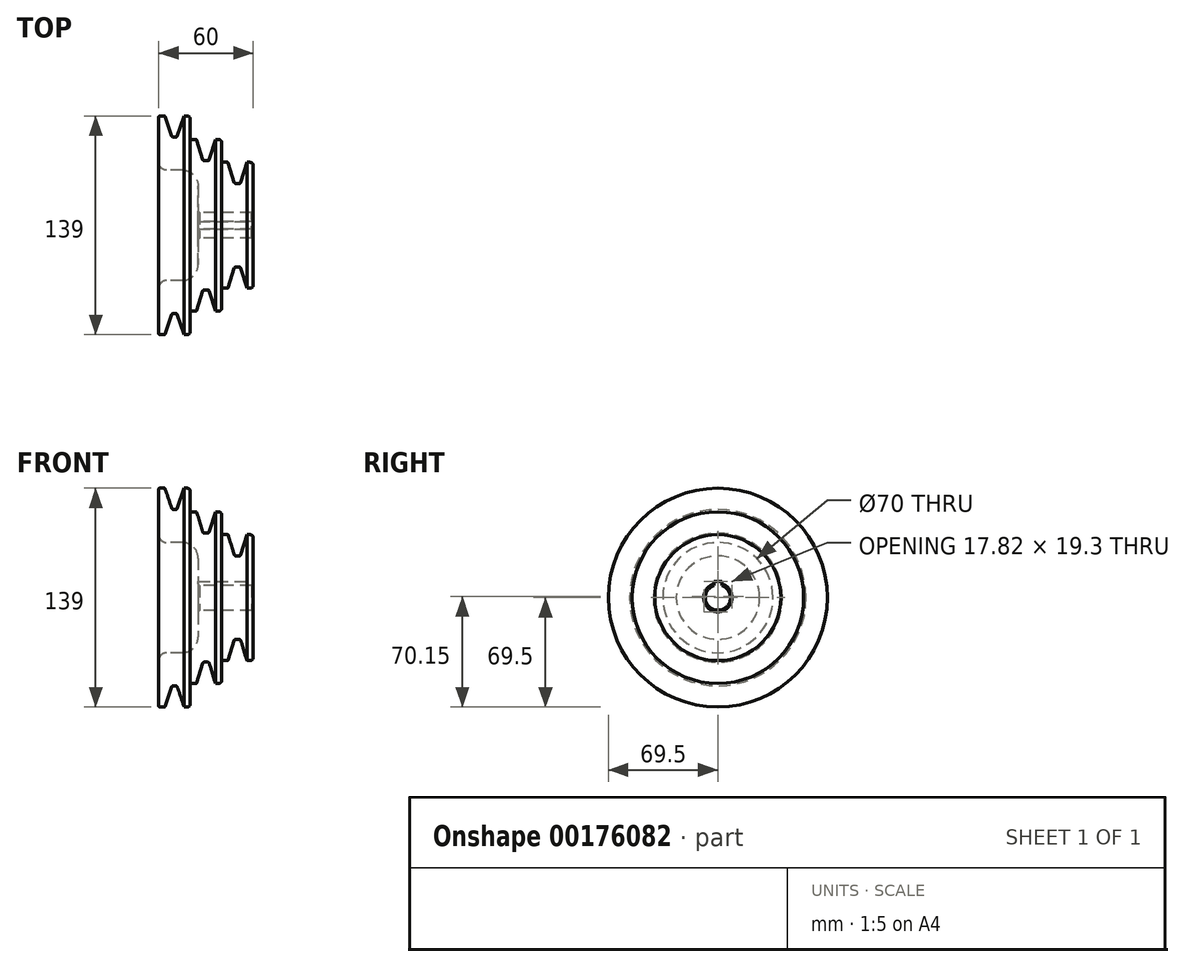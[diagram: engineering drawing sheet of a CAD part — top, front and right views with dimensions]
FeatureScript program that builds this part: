
annotation { "Feature Type Name" : "Feature", "Feature Type Description" : "" }
export const myFeature = defineFeature(function(context is Context, id is Id, definition is map)
    precondition{}
    {
        {
            var Q0;
            Q0=qCreatedBy(makeId("Front.planeOp"),FACE);
            var sketch = newSketch(context, id + "F0", { "sketchPlane" : qUnion([Q0])});
            skLineSegment(sketch, "E0", {"start": v(60, 8) * mm, "end": v(25, 8) * mm});
            skLineSegment(sketch, "E1", {"start": v(25, 8) * mm, "end": v(25, 35) * mm});
            skLineSegment(sketch, "E2", {"start": v(25, 35) * mm, "end": v(0, 35) * mm});
            skLineSegment(sketch, "E3", {"start": v(0, 35) * mm, "end": v(0, 69.5) * mm});
            skLineSegment(sketch, "E4", {"start": v(0, 69.5) * mm, "end": v(20, 69.5) * mm});
            skLineSegment(sketch, "E5", {"start": v(20, 69.5) * mm, "end": v(20, 54.5) * mm});
            skLineSegment(sketch, "E6", {"start": v(20, 54.5) * mm, "end": v(40, 54.5) * mm});
            skLineSegment(sketch, "E7", {"start": v(40, 54.5) * mm, "end": v(40, 40) * mm});
            skLineSegment(sketch, "E8", {"start": v(40, 40) * mm, "end": v(60, 40) * mm});
            skLineSegment(sketch, "E9", {"start": v(60, 40) * mm, "end": v(60, 8) * mm});
            skLineSegment(sketch, "E10", {"start": v(0, 0) * mm, "end": v(60.5, 0) * mm});
            skSolve(sketch);
        }
        {
            var Q0;
            Q0 = qSketchRegion(id + "F0", true);
            var Q1;
            Q1=sQuery(id+"F0.wireOp",EDGE,"E10");
            revolve(context, id + "F1", {"entities" : qUnion([Q0]), "axis" : qUnion([Q1]), "revolveType" : RevolveType.FULL});
        }
        {
            var Q0;
            Q0=qCreatedBy(makeId("Front.planeOp"),FACE);
            var sketch = newSketch(context, id + "F2", { "sketchPlane" : qUnion([Q0])});
            skLineSegment(sketch, "E11", {"start": v(3.85, 69.5) * mm, "end": v(16.15, 69.5) * mm});
            skLineSegment(sketch, "E12", {"start": v(16.15, 69.5) * mm, "end": v(11.5, 56) * mm});
            skLineSegment(sketch, "E13", {"start": v(11.5, 56) * mm, "end": v(8.5, 56) * mm});
            skLineSegment(sketch, "E14", {"start": v(8.5, 56) * mm, "end": v(3.85, 69.5) * mm});
            skLineSegment(sketch, "E15", {"start": v(10, 69.5) * mm, "end": v(10, 56) * mm});
            skLineSegment(sketch, "E16", {"start": v(5.4, 65) * mm, "end": v(14.6, 65) * mm});
            skLineSegment(sketch, "E17", {"start": v(0, 0) * mm, "end": v(23.75, 0) * mm});
            skSolve(sketch);
        }
        {
            var Q0;
            Q0 = qSketchRegion(id + "F2", true);
            var Q1;
            Q1=sQuery(id+"F2.wireOp",EDGE,"E17");
            revolve(context, id + "F3", {"operationType" : NewBodyOperationType.REMOVE, "entities" : qUnion([Q0]), "axis" : qUnion([Q1]), "revolveType" : RevolveType.FULL, "oppositeDirection" : true});
        }
        {
            var Q0;
            Q0=qCreatedBy(makeId("Front.planeOp"),FACE);
            var sketch = newSketch(context, id + "F4", { "sketchPlane" : qUnion([Q0])});
            skLineSegment(sketch, "E18", {"start": v(24.02, 54.5) * mm, "end": v(35.98, 54.5) * mm});
            skLineSegment(sketch, "E19", {"start": v(35.98, 54.5) * mm, "end": v(31.85, 41) * mm});
            skLineSegment(sketch, "E20", {"start": v(31.85, 41) * mm, "end": v(28.15, 41) * mm});
            skLineSegment(sketch, "E21", {"start": v(28.15, 41) * mm, "end": v(24.02, 54.5) * mm});
            skLineSegment(sketch, "E22", {"start": v(30, 54.5) * mm, "end": v(30, 41) * mm});
            skLineSegment(sketch, "E23", {"start": v(25.4, 50) * mm, "end": v(34.6, 50) * mm});
            skLineSegment(sketch, "E24", {"start": v(0, 0) * mm, "end": v(40.75, 0) * mm});
            skSolve(sketch);
        }
        {
            var Q0;
            Q0 = qSketchRegion(id + "F4", true);
            var Q1;
            Q1=sQuery(id+"F4.wireOp",EDGE,"E24");
            revolve(context, id + "F5", {"operationType" : NewBodyOperationType.REMOVE, "entities" : qUnion([Q0]), "axis" : qUnion([Q1]), "revolveType" : RevolveType.FULL});
        }
        {
            var Q0;
            Q0=qCreatedBy(makeId("Front.planeOp"),FACE);
            var sketch = newSketch(context, id + "F6", { "sketchPlane" : qUnion([Q0])});
            skLineSegment(sketch, "E25", {"start": v(44.02, 40) * mm, "end": v(55.98, 40) * mm});
            skLineSegment(sketch, "E26", {"start": v(55.98, 40) * mm, "end": v(51.85, 26.5) * mm});
            skLineSegment(sketch, "E27", {"start": v(51.85, 26.5) * mm, "end": v(48.15, 26.5) * mm});
            skLineSegment(sketch, "E28", {"start": v(48.15, 26.5) * mm, "end": v(44.02, 40) * mm});
            skLineSegment(sketch, "E29", {"start": v(50, 40) * mm, "end": v(50, 26.5) * mm});
            skLineSegment(sketch, "E30", {"start": v(45.4, 35.5) * mm, "end": v(54.6, 35.5) * mm});
            skLineSegment(sketch, "E31", {"start": v(0, 0) * mm, "end": v(19.74, 0) * mm});
            skSolve(sketch);
        }
        {
            var Q0;
            Q0 = qSketchRegion(id + "F6", true);
            var Q1;
            Q1=sQuery(id+"F6.wireOp",EDGE,"E31");
            revolve(context, id + "F7", {"operationType" : NewBodyOperationType.REMOVE, "entities" : qUnion([Q0]), "axis" : qUnion([Q1]), "revolveType" : RevolveType.FULL, "oppositeDirection" : true});
        }
        {
            var Q0;
            Q0=makeQuery(id+"F1.opRevolve","SWEPT_EDGE",EDGE,{"disambiguationData":[OSD([sQuery(id+"F0.wireOp",EDGE,"E3"),sQuery(id+"F0.wireOp",EDGE,"E4")])]});
            var Q1;
            Q1=makeQuery(id+"F3.boolean.opBoolean","COPY",EDGE,{"derivedFrom":makeQuery(id+"F3.opRevolve","SWEPT_EDGE",EDGE,{"disambiguationData":[OSD([sQuery(id+"F2.wireOp",EDGE,"E11"),sQuery(id+"F2.wireOp",EDGE,"E14")])]})});
            var Q2;
            Q2=makeQuery(id+"F3.boolean.opBoolean","COPY",EDGE,{"derivedFrom":makeQuery(id+"F3.opRevolve","SWEPT_EDGE",EDGE,{"disambiguationData":[OSD([sQuery(id+"F2.wireOp",EDGE,"E11"),sQuery(id+"F2.wireOp",EDGE,"E12")])]})});
            var Q3;
            Q3=makeQuery(id+"F1.opRevolve","SWEPT_EDGE",EDGE,{"disambiguationData":[OSD([sQuery(id+"F0.wireOp",EDGE,"E5"),sQuery(id+"F0.wireOp",EDGE,"E6")])]});
            var Q4;
            Q4=makeQuery(id+"F5.boolean.opBoolean","COPY",EDGE,{"derivedFrom":makeQuery(id+"F5.opRevolve","SWEPT_EDGE",EDGE,{"disambiguationData":[OSD([sQuery(id+"F4.wireOp",EDGE,"E18"),sQuery(id+"F4.wireOp",EDGE,"E21")])]})});
            var Q5;
            Q5=makeQuery(id+"F5.boolean.opBoolean","COPY",EDGE,{"derivedFrom":makeQuery(id+"F5.opRevolve","SWEPT_EDGE",EDGE,{"disambiguationData":[OSD([sQuery(id+"F4.wireOp",EDGE,"E18"),sQuery(id+"F4.wireOp",EDGE,"E19")])]})});
            var Q6;
            Q6=makeQuery(id+"F1.opRevolve","SWEPT_EDGE",EDGE,{"disambiguationData":[OSD([sQuery(id+"F0.wireOp",EDGE,"E7"),sQuery(id+"F0.wireOp",EDGE,"E8")])]});
            var Q7;
            Q7=makeQuery(id+"F7.boolean.opBoolean","COPY",EDGE,{"derivedFrom":makeQuery(id+"F7.opRevolve","SWEPT_EDGE",EDGE,{"disambiguationData":[OSD([sQuery(id+"F6.wireOp",EDGE,"E25"),sQuery(id+"F6.wireOp",EDGE,"E28")])]})});
            var Q8;
            Q8=makeQuery(id+"F7.boolean.opBoolean","COPY",EDGE,{"derivedFrom":makeQuery(id+"F7.opRevolve","SWEPT_EDGE",EDGE,{"disambiguationData":[OSD([sQuery(id+"F6.wireOp",EDGE,"E25"),sQuery(id+"F6.wireOp",EDGE,"E26")])]})});
            fillet(context, id + "F8", {"entities" : qUnion([Q0, Q1, Q2, Q3, Q4, Q5, Q6, Q7, Q8]), "radius" : 0.5 * mm, "tangentPropagation" : true, "allowEdgeOverflow" : false});
        }
        {
            var Q0;
            Q0=makeQuery(id+"F1.opRevolve","SWEPT_EDGE",EDGE,{"disambiguationData":[OSD([sQuery(id+"F0.wireOp",EDGE,"E4"),sQuery(id+"F0.wireOp",EDGE,"E5")])]});
            var Q1;
            Q1=makeQuery(id+"F1.opRevolve","SWEPT_EDGE",EDGE,{"disambiguationData":[OSD([sQuery(id+"F0.wireOp",EDGE,"E6"),sQuery(id+"F0.wireOp",EDGE,"E7")])]});
            var Q2;
            Q2=makeQuery(id+"F1.opRevolve","SWEPT_EDGE",EDGE,{"disambiguationData":[OSD([sQuery(id+"F0.wireOp",EDGE,"E8"),sQuery(id+"F0.wireOp",EDGE,"E9")])]});
            fillet(context, id + "F9", {"entities" : qUnion([Q0, Q1, Q2]), "radius" : 2 * mm, "tangentPropagation" : true, "allowEdgeOverflow" : false});
        }
        {
            var Q0;
            Q0=makeQuery(id+"F3.boolean.opBoolean","COPY",EDGE,{"derivedFrom":makeQuery(id+"F3.opRevolve","SWEPT_EDGE",EDGE,{"disambiguationData":[OSD([sQuery(id+"F2.wireOp",EDGE,"E13"),sQuery(id+"F2.wireOp",EDGE,"E14")])]})});
            var Q1;
            Q1=makeQuery(id+"F3.boolean.opBoolean","COPY",EDGE,{"derivedFrom":makeQuery(id+"F3.opRevolve","SWEPT_EDGE",EDGE,{"disambiguationData":[OSD([sQuery(id+"F2.wireOp",EDGE,"E12"),sQuery(id+"F2.wireOp",EDGE,"E13")])]})});
            var Q2;
            Q2=makeQuery(id+"F5.boolean.opBoolean","COPY",EDGE,{"derivedFrom":makeQuery(id+"F5.opRevolve","SWEPT_EDGE",EDGE,{"disambiguationData":[OSD([sQuery(id+"F4.wireOp",EDGE,"E20"),sQuery(id+"F4.wireOp",EDGE,"E21")])]})});
            var Q3;
            Q3=makeQuery(id+"F5.boolean.opBoolean","COPY",EDGE,{"derivedFrom":makeQuery(id+"F5.opRevolve","SWEPT_EDGE",EDGE,{"disambiguationData":[OSD([sQuery(id+"F4.wireOp",EDGE,"E19"),sQuery(id+"F4.wireOp",EDGE,"E20")])]})});
            var Q4;
            Q4=makeQuery(id+"F7.boolean.opBoolean","COPY",EDGE,{"derivedFrom":makeQuery(id+"F7.opRevolve","SWEPT_EDGE",EDGE,{"disambiguationData":[OSD([sQuery(id+"F6.wireOp",EDGE,"E27"),sQuery(id+"F6.wireOp",EDGE,"E28")])]})});
            var Q5;
            Q5=makeQuery(id+"F7.boolean.opBoolean","COPY",EDGE,{"derivedFrom":makeQuery(id+"F7.opRevolve","SWEPT_EDGE",EDGE,{"disambiguationData":[OSD([sQuery(id+"F6.wireOp",EDGE,"E26"),sQuery(id+"F6.wireOp",EDGE,"E27")])]})});
            fillet(context, id + "F10", {"entities" : qUnion([Q0, Q1, Q2, Q3, Q4, Q5]), "radius" : 1 * mm, "tangentPropagation" : true, "allowEdgeOverflow" : false});
        }
        {
            var Q0;
            Q0=makeQuery(id+"F1.opRevolve","SWEPT_EDGE",EDGE,{"disambiguationData":[OSD([sQuery(id+"F0.wireOp",EDGE,"E1"),sQuery(id+"F0.wireOp",EDGE,"E2")])]});
            fillet(context, id + "F11", {"entities" : qUnion([Q0]), "radius" : 10 * mm, "tangentPropagation" : true, "allowEdgeOverflow" : false});
        }
        {
            var Q0;
            Q0=makeQuery(id+"F1.opRevolve","SWEPT_EDGE",EDGE,{"disambiguationData":[OSD([sQuery(id+"F0.wireOp",EDGE,"E2"),sQuery(id+"F0.wireOp",EDGE,"E3")])]});
            fillet(context, id + "F12", {"entities" : qUnion([Q0]), "radius" : 5 * mm, "tangentPropagation" : true, "allowEdgeOverflow" : false});
        }
        {
            var Q0;
            Q0=makeQuery(id+"F1.opRevolve","SWEPT_EDGE",EDGE,{"disambiguationData":[OSD([sQuery(id+"F0.wireOp",EDGE,"E0"),sQuery(id+"F0.wireOp",EDGE,"E1")])]});
            var Q1;
            Q1=makeQuery(id+"F1.opRevolve","SWEPT_EDGE",EDGE,{"disambiguationData":[OSD([sQuery(id+"F0.wireOp",EDGE,"E0"),sQuery(id+"F0.wireOp",EDGE,"E9")])]});
            chamfer(context, id + "F13", {"entities" : qUnion([Q0, Q1]), "width" : 1 * mm, "tangentPropagation" : true});
        }
        {
            var Q0;
            Q0=makeQuery(id+"F1.opRevolve","SWEPT_FACE",FACE,{"disambiguationData":[OSD([sQuery(id+"F0.wireOp",EDGE,"E9")])]});
            var sketch = newSketch(context, id + "F14", { "sketchPlane" : qUnion([Q0])});
            skLineSegment(sketch, "E32.bottom", {"start": v(-2.5, 10.3) * mm, "end": v(2.5, 10.3) * mm});
            skLineSegment(sketch, "E32.top", {"start": v(-2.5, 5.84) * mm, "end": v(2.5, 5.84) * mm});
            skLineSegment(sketch, "E32.left", {"start": v(-2.5, 10.3) * mm, "end": v(-2.5, 5.84) * mm});
            skLineSegment(sketch, "E32.right", {"start": v(2.5, 10.3) * mm, "end": v(2.5, 5.84) * mm});
            skLineSegment(sketch, "E33", {"start": v(0, 10.3) * mm, "end": v(0, 5.84) * mm});
            skSolve(sketch);
        }
        {
            var Q0;
            Q0 = qSketchRegion(id + "F14", true);
            extrude(context, id + "F15", {"entities" : qUnion([Q0]), "operationType" : NewBodyOperationType.REMOVE, "endBound" : BoundingType.THROUGH_ALL, "oppositeDirection" : true, "depth" : 25 * mm});
        }
    });
